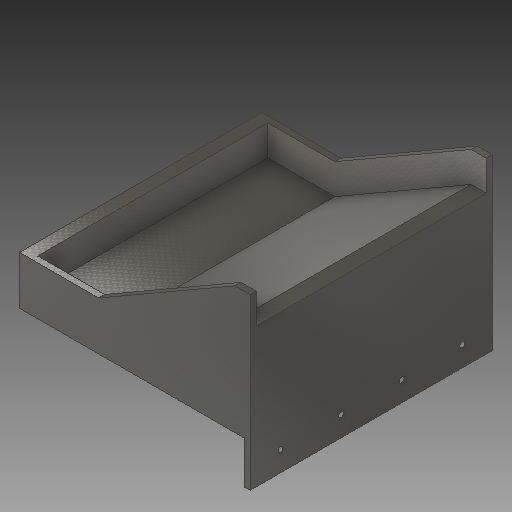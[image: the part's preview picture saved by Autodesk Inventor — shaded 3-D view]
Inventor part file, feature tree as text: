
AUTODESK INVENTOR PART (.ipt)
format: ipt  version: 2019 (Build 230136000, 136)  size: 262,144 bytes
history: native  units: mm
features: sketch x7, extrude x6, plane x2, mirror x1, hole x1, pattern_linear x1
ambient origin geometry x8: Origin, YZ Plane, XZ Plane, XY Plane, X Axis, Y Axis, Z Axis, Center Point
bodies: Solid1 (feature_tree)
feature tree (18):
  extrude  "Extrusion1"  Depth=260.0mm
  extrude  "Extrusion8"  Depth=200.0mm TaperAngle=0.0deg
  extrude  "Extrusion9"  Depth=30.0mm TaperAngle=0.0deg
  extrude  "Extrusion10"  Depth=20.0mm
  extrude  "Extrusion11"  Depth=50.0mm
  plane  "Work Plane2"
  mirror  "Mirror1"
  extrude  "Extrusion12"  Depth=10.0mm TaperAngle=0.0deg
  hole  "Hole1"  [1 undecoded]
  pattern_linear  "Rectangular Pattern1"  Count1=7 Spacing1=0.0mm
  sketch  "Sketch1"  dims[d4=30.0deg d5=260.0mm]
  sketch  "Sketch8"  dims[d6=25.0mm d7=200.0mm d8=0.0mm]
  sketch  "Sketch9"  dims[d24=200.0mm d25=0.0mm d28=30.0mm d29=0.0mm]
  sketch  "Sketch10"  dims[d30=120.0mm d31=0.0mm d32=20.0mm]
  sketch  "Sketch11"  dims[d33=50.0mm d34=0.0mm d35=50.0mm]
  plane  "Work Plane1"
  sketch  "Sketch12"  dims[d36=50.0mm d37=10.0mm d38=0.0mm]
  sketch  "Sketch13"  dims[d39=5.0mm d40=10.0mm d41=70.0mm d42=0.0mm d43=50.0mm d44=37.0mm d45=8.376mm d46=20.0mm d47=4.0mm d48=2.0mm d49=90.0deg d50=27.3mm d51=20.594885mm d52=40.0mm d54=100.0mm]
note: 1 required parameter value undecoded (feature->parameter linkage not recoverable at this tier; creation-order binding heuristic only, values carry confidence <= 0.55)
